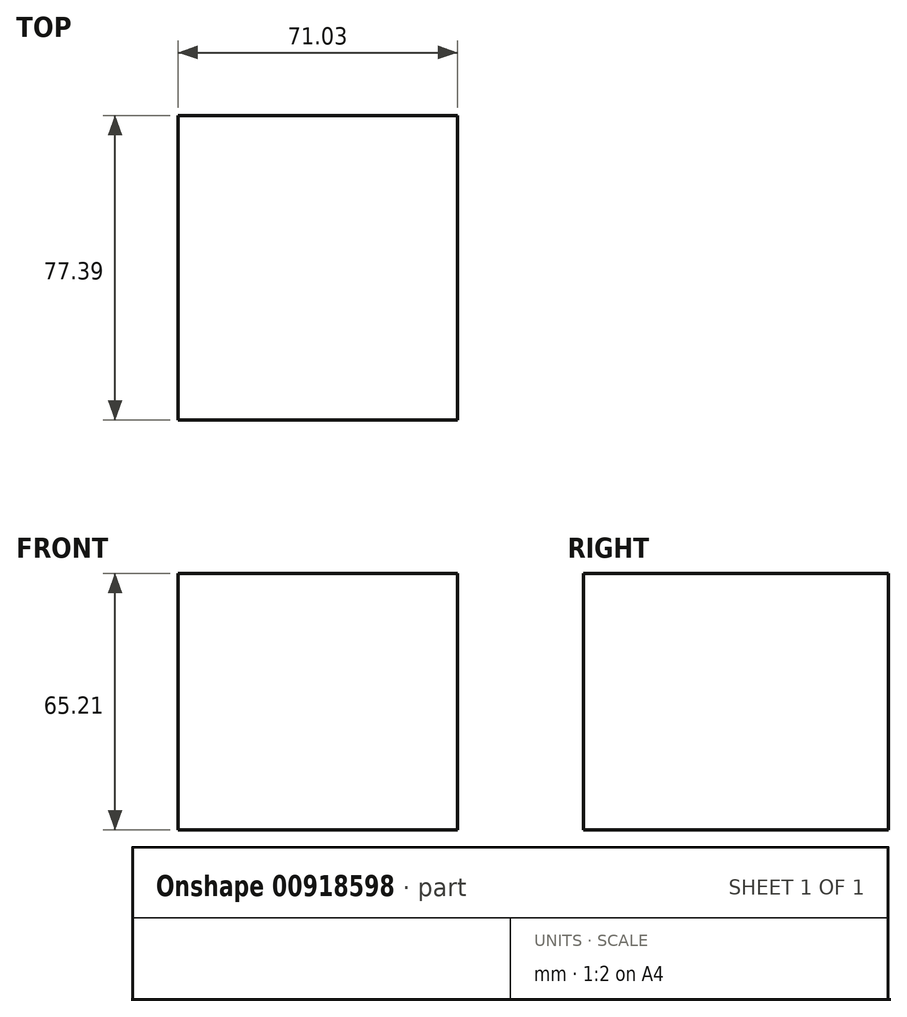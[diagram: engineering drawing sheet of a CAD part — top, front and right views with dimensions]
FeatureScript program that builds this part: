
annotation { "Feature Type Name" : "Feature", "Feature Type Description" : "" }
export const myFeature = defineFeature(function(context is Context, id is Id, definition is map)
    precondition{}
    {
        {
            var Q0;
            Q0=qCreatedBy(makeId("Top.planeOp"),FACE);
            var sketch = newSketch(context, id + "F0", { "sketchPlane" : qUnion([Q0])});
            skLineSegment(sketch, "E0.bottom", {"start": v(55, 0) * mm, "end": v(-16.03, 0) * mm});
            skLineSegment(sketch, "E0.top", {"start": v(55, 77.39) * mm, "end": v(-16.03, 77.39) * mm});
            skLineSegment(sketch, "E0.left", {"start": v(55, 0) * mm, "end": v(55, 77.39) * mm});
            skLineSegment(sketch, "E0.right", {"start": v(-16.03, 0) * mm, "end": v(-16.03, 77.39) * mm});
            skSolve(sketch);
        }
        {
            var Q0;
            Q0 = qSketchRegion(id + "F0", true);
            extrude(context, id + "F1", {"entities" : qUnion([Q0]), "depth" : 65.2 * mm, "offsetDistance" : 25.4 * mm});
        }
    });
